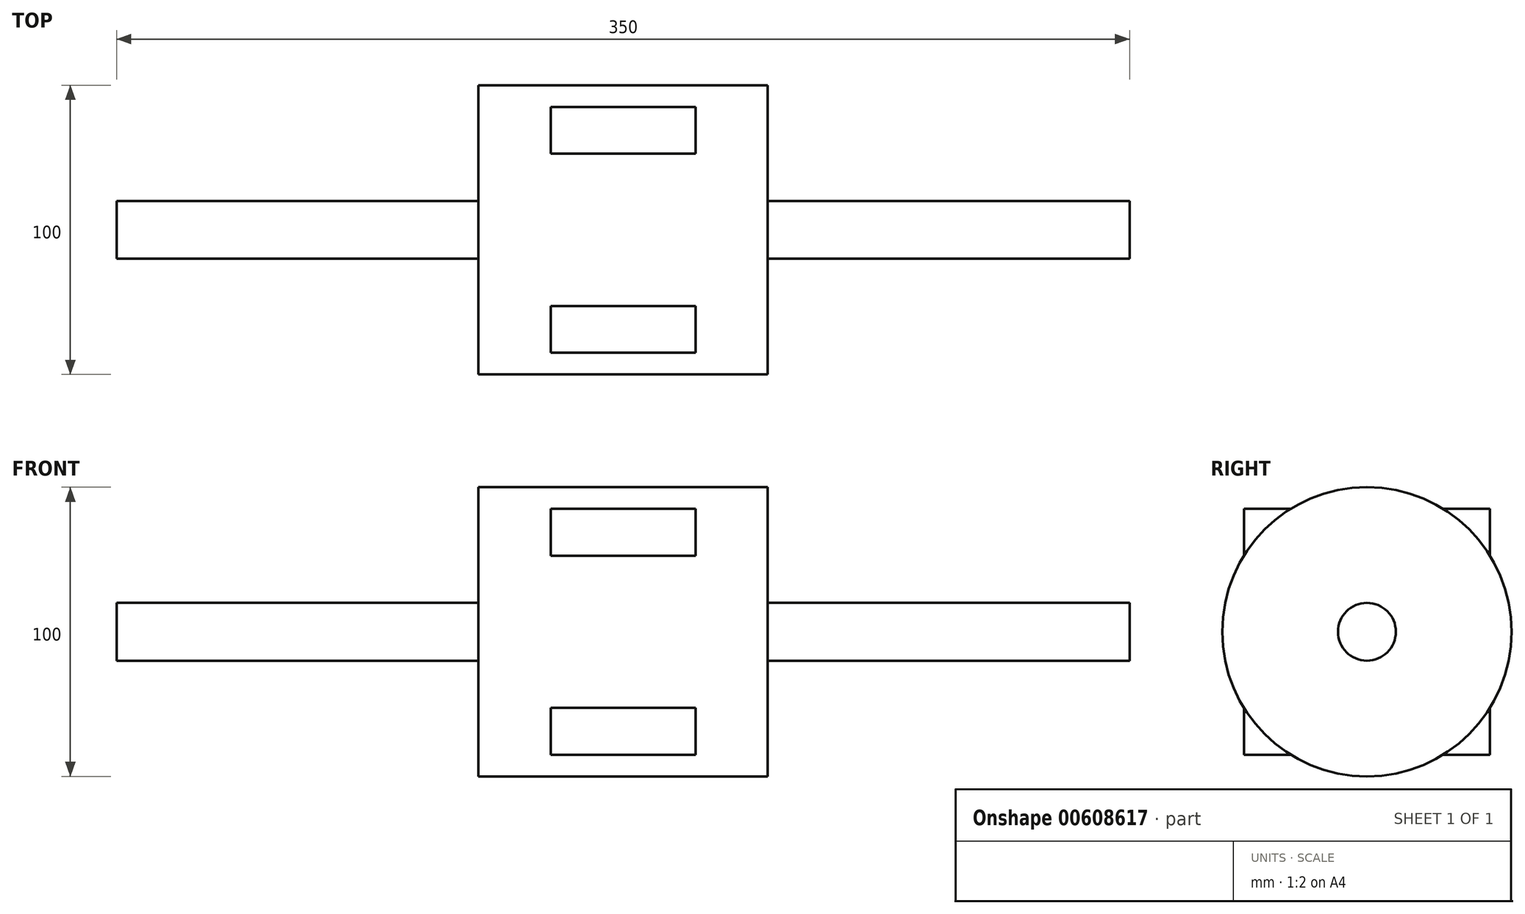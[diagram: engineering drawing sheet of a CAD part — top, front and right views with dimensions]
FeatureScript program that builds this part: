
annotation { "Feature Type Name" : "Feature", "Feature Type Description" : "" }
export const myFeature = defineFeature(function(context is Context, id is Id, definition is map)
    precondition{}
    {
        {
            var Q0;
            Q0=qCreatedBy(makeId("Right.planeOp"),FACE);
            var sketch = newSketch(context, id + "F0", { "sketchPlane" : qUnion([Q0])});
            skCircle(sketch, "E0", {"center": v(0, 0) * mm, "radius": 10 * mm});
            skSolve(sketch);
        }
        {
            var Q0;
            Q0 = qSketchRegion(id + "F0", true);
            extrude(context, id + "F1", {"entities" : qUnion([Q0]), "depth" : 125 * mm, "offsetDistance" : 25 * mm});
        }
        {
            var Q0;
            Q0=makeQuery(id+"F1.opExtrude","CAP_FACE",FACE,{"disambiguationData":[OSD([sQuery(id+"F0.wireOp",EDGE,"E0")])],"isStart":false});
            var sketch = newSketch(context, id + "F2", { "sketchPlane" : qUnion([Q0])});
            skCircle(sketch, "E1", {"center": v(0, 0) * mm, "radius": 50 * mm});
            skSolve(sketch);
        }
        {
            var Q0;
            Q0=makeQuery(id+"F2.imprint","IMPRINT",FACE,{"disambiguationData":[TD([[makeQuery(id+"F2.imprint","IMPRINT",EDGE,{"derivedFrom":sQuery(id+"F2.wireOp",EDGE,"E1")}),1.0]])]});
            var Q1;
            Q1=makeQuery(id+"F2.imprint","IMPRINT",FACE,{"disambiguationData":[TD([[makeQuery(id+"F2.imprint","IMPRINT",EDGE,{"derivedFrom":makeQuery(id+"F1.opExtrude","CAP_EDGE",EDGE,{"disambiguationData":[OSD([sQuery(id+"F0.wireOp",EDGE,"E0")])],"isStart":false})}),1.0]])]});
            extrude(context, id + "F3", {"entities" : qUnion([Q0, Q1]), "operationType" : NewBodyOperationType.ADD, "depth" : 50 * mm, "offsetDistance" : 25 * mm});
        }
        {
            var Q0;
            Q0=makeQuery(id+"F3.opExtrude","CAP_FACE",FACE,{"disambiguationData":[OSD([sQuery(id+"F2.wireOp",EDGE,"E1")])],"isStart":false});
            var sketch = newSketch(context, id + "F4", { "sketchPlane" : qUnion([Q0])});
            skPoint(sketch, "E2.middle", {"position": v(0, 0) * mm});
            skLineSegment(sketch, "E3.bottom", {"start": v(42.5, -42.5) * mm, "end": v(-42.5, -42.5) * mm});
            skLineSegment(sketch, "E3.top", {"start": v(42.5, 42.5) * mm, "end": v(-42.5, 42.5) * mm});
            skLineSegment(sketch, "E3.left", {"start": v(42.5, -42.5) * mm, "end": v(42.5, 42.5) * mm});
            skLineSegment(sketch, "E3.right", {"start": v(-42.5, -42.5) * mm, "end": v(-42.5, 42.5) * mm});
            skSolve(sketch);
        }
        {
            var Q0;
            {var subQ0=sQuery(id+"F4.wireOp",EDGE,"E3.right");var subQ1=sQuery(id+"F4.wireOp",EDGE,"E3.top");var subQ2=makeQuery(id+"F4.imprint","INTERSECT",VERTEX,{"derivedFrom":[subQ1,subQ0]});Q0=makeQuery(id+"F4.imprint","IMPRINT",FACE,{"disambiguationData":[TD([[makeQuery(id+"F4.imprint","IMPRINT",EDGE,{"disambiguationData":[TD([[subQ2,1.0]])],"derivedFrom":subQ1}),1.0]])]});}
            var Q1;
            {var subQ0=sQuery(id+"F4.wireOp",EDGE,"E3.left");var subQ1=sQuery(id+"F4.wireOp",EDGE,"E3.top");var subQ2=makeQuery(id+"F4.imprint","INTERSECT",VERTEX,{"derivedFrom":[subQ1,subQ0]});Q1=makeQuery(id+"F4.imprint","IMPRINT",FACE,{"disambiguationData":[TD([[makeQuery(id+"F4.imprint","IMPRINT",EDGE,{"disambiguationData":[TD([[subQ2,-1.0]])],"derivedFrom":subQ1}),1.0]])]});}
            var Q2;
            {var subQ0=sQuery(id+"F4.wireOp",EDGE,"E3.left");var subQ1=sQuery(id+"F4.wireOp",EDGE,"E3.bottom");var subQ2=makeQuery(id+"F4.imprint","INTERSECT",VERTEX,{"derivedFrom":[subQ1,subQ0]});Q2=makeQuery(id+"F4.imprint","IMPRINT",FACE,{"disambiguationData":[TD([[makeQuery(id+"F4.imprint","IMPRINT",EDGE,{"disambiguationData":[TD([[subQ2,-1.0]])],"derivedFrom":subQ1}),-1.0]])]});}
            var Q3;
            {var subQ0=sQuery(id+"F4.wireOp",EDGE,"E3.right");var subQ1=sQuery(id+"F4.wireOp",EDGE,"E3.bottom");var subQ2=makeQuery(id+"F4.imprint","INTERSECT",VERTEX,{"derivedFrom":[subQ1,subQ0]});Q3=makeQuery(id+"F4.imprint","IMPRINT",FACE,{"disambiguationData":[TD([[makeQuery(id+"F4.imprint","IMPRINT",EDGE,{"disambiguationData":[TD([[subQ2,1.0]])],"derivedFrom":subQ1}),-1.0]])]});}
            var Q4;
            {var subQ1=makeQuery(id+"F3.opExtrude","CAP_EDGE",EDGE,{"disambiguationData":[OSD([sQuery(id+"F2.wireOp",EDGE,"E1")])],"isStart":false});var subQ10=sQuery(id+"F4.wireOp",EDGE,"E3.bottom");var subQ11=makeQuery(id+"F4.imprint","INTERSECT",VERTEX,{"disambiguationData":[OD(0.0)],"derivedFrom":[subQ1,subQ10]});Q4=makeQuery(id+"F4.imprint","IMPRINT",FACE,{"disambiguationData":[TD([[makeQuery(id+"F4.imprint","IMPRINT",EDGE,{"disambiguationData":[TD([[subQ11,-1.0]])],"derivedFrom":subQ10}),-1.0]])]});}
            extrude(context, id + "F5", {"entities" : qUnion([Q0, Q1, Q2, Q3, Q4]), "operationType" : NewBodyOperationType.ADD, "oppositeDirection" : true, "depth" : 25 * mm, "offsetDistance" : 25 * mm});
        }
        {
            var Q0;
            Q0=makeQuery(id+"F1.opExtrude","SWEPT_BODY",BODY,{"disambiguationData":[OSD([sQuery(id+"F0.wireOp",EDGE,"E0")])]});
            var Q1;
            Q1=makeQuery(id+"F5.boolean.opBoolean","MERGE",FACE,{"derivedFrom":[makeQuery(id+"F3.opExtrude","CAP_FACE",FACE,{"disambiguationData":[OSD([sQuery(id+"F2.wireOp",EDGE,"E1")])],"isStart":false}),makeQuery(id+"F5.opExtrude","CAP_FACE",FACE,{"disambiguationData":[OSD([sQuery(id+"F4.wireOp",EDGE,"E3.bottom"),sQuery(id+"F4.wireOp",EDGE,"E3.top"),sQuery(id+"F4.wireOp",EDGE,"E3.left"),sQuery(id+"F4.wireOp",EDGE,"E3.right")])],"isStart":true})]});
            mirror(context, id + "F6", {"operationType" : NewBodyOperationType.ADD, "entities" : qUnion([Q0]), "mirrorPlane" : qUnion([Q1])});
        }
    });
